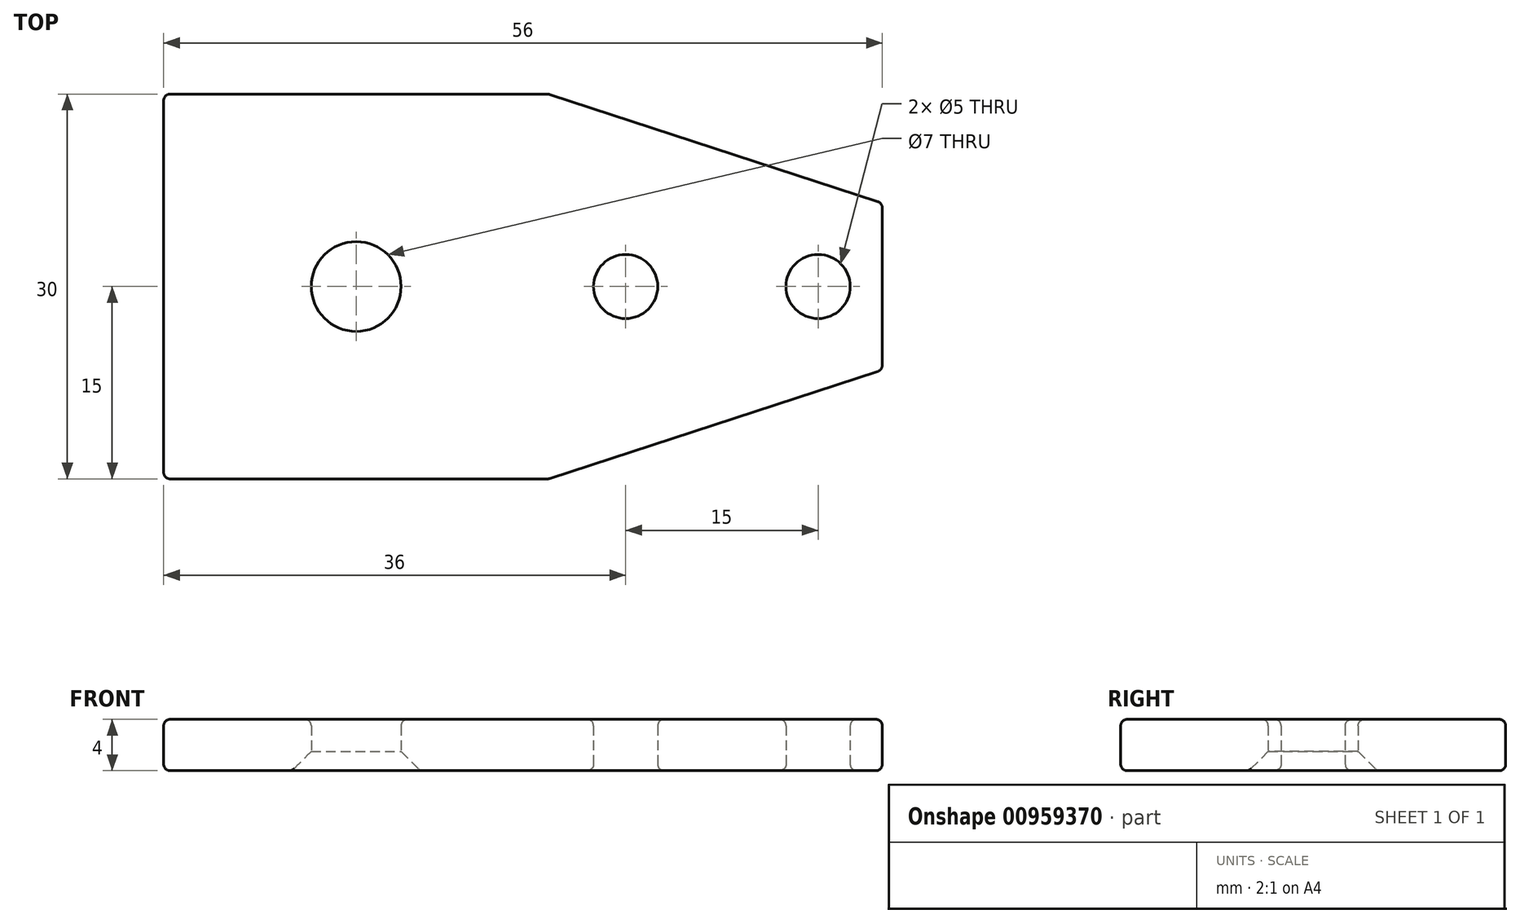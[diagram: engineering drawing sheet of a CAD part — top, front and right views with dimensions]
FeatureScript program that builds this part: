
annotation { "Feature Type Name" : "Feature", "Feature Type Description" : "" }
export const myFeature = defineFeature(function(context is Context, id is Id, definition is map)
    precondition{}
    {
        {
            var Q0;
            Q0=qCreatedBy(makeId("Top.planeOp"),FACE);
            var sketch = newSketch(context, id + "F0", { "sketchPlane" : qUnion([Q0])});
            skLineSegment(sketch, "E0.bottom", {"start": v(15, -15) * mm, "end": v(-15, -15) * mm});
            skLineSegment(sketch, "E0.top", {"start": v(15, 15) * mm, "end": v(-15, 15) * mm});
            skLineSegment(sketch, "E0.left", {"start": v(15, -15) * mm, "end": v(15, 15) * mm});
            skLineSegment(sketch, "E0.right", {"start": v(-15, -15) * mm, "end": v(-15, 15) * mm});
            skPoint(sketch, "E0.middle", {"position": v(0, 0) * mm});
            skLineSegment(sketch, "E1", {"start": v(15, -15) * mm, "end": v(41, -6.5) * mm});
            skLineSegment(sketch, "E2", {"start": v(41, -6.5) * mm, "end": v(41, 6.5) * mm});
            skLineSegment(sketch, "E3", {"start": v(41, 6.5) * mm, "end": v(15, 15) * mm});
            skPoint(sketch, "E4", {"position": v(41, 0) * mm});
            skLineSegment(sketch, "E5", {"start": v(41, 0) * mm, "end": v(0, 0) * mm, "construction": true});
            skPoint(sketch, "E6", {"position": v(36, 0) * mm});
            skPoint(sketch, "E7", {"position": v(21, 0) * mm});
            skSolve(sketch);
        }
        {
            var Q0;
            Q0=makeQuery(id+"F0.imprint","IMPRINT",FACE,{"disambiguationData":[TD([[makeQuery(id+"F0.imprint","IMPRINT",EDGE,{"derivedFrom":sQuery(id+"F0.wireOp",EDGE,"E0.bottom")}),-1.0]])]});
            var Q1;
            Q1=makeQuery(id+"F0.imprint","IMPRINT",FACE,{"disambiguationData":[TD([[makeQuery(id+"F0.imprint","IMPRINT",EDGE,{"derivedFrom":sQuery(id+"F0.wireOp",EDGE,"E0.left")}),-1.0]])]});
            extrude(context, id + "F1", {"entities" : qUnion([Q0, Q1]), "depth" : 4 * mm, "offsetDistance" : 25 * mm});
        }
        {
            var Q0;
            Q0=sQuery(id+"F0.wireOp",VERTEX,"E0.middle");
            var Q1;
            Q1=makeQuery(id+"F1.opExtrude","SWEPT_BODY",BODY,{"disambiguationData":[OSD([sQuery(id+"F0.wireOp",EDGE,"E0.bottom"),sQuery(id+"F0.wireOp",EDGE,"E0.top"),sQuery(id+"F0.wireOp",EDGE,"E0.right"),sQuery(id+"F0.wireOp",EDGE,"E1"),sQuery(id+"F0.wireOp",EDGE,"E2"),sQuery(id+"F0.wireOp",EDGE,"E3")])]});
            hole(context, id + "F2", {"style" : HoleStyle.C_SINK, "endStyle" : HoleEndStyle.THROUGH, "oppositeDirection" : true, "holeDiameter" : 7 * mm, "cSinkDiameter" : 10 * mm, "cSinkAngle" : 90 * degree, "majorDiameter" : 5 * mm, "isTappedThrough" : true, "tappedDepth" : 12 * mm, "tapClearance" : 3, "locations" : qUnion([Q0]), "scope" : qUnion([Q1])});
        }
        {
            var Q0;
            Q0=sQuery(id+"F0.wireOp",VERTEX,"E7");
            var Q1;
            Q1=sQuery(id+"F0.wireOp",VERTEX,"E6");
            var Q2;
            Q2=makeQuery(id+"F1.opExtrude","SWEPT_BODY",BODY,{"disambiguationData":[OSD([sQuery(id+"F0.wireOp",EDGE,"E0.bottom"),sQuery(id+"F0.wireOp",EDGE,"E0.top"),sQuery(id+"F0.wireOp",EDGE,"E0.right"),sQuery(id+"F0.wireOp",EDGE,"E1"),sQuery(id+"F0.wireOp",EDGE,"E2"),sQuery(id+"F0.wireOp",EDGE,"E3")])]});
            hole(context, id + "F3", {"style" : HoleStyle.SIMPLE, "endStyle" : HoleEndStyle.THROUGH, "oppositeDirection" : true, "holeDiameter" : 5 * mm, "majorDiameter" : 5 * mm, "isTappedThrough" : true, "tappedDepth" : 12 * mm, "tapClearance" : 3, "locations" : qUnion([Q0, Q1]), "scope" : qUnion([Q2])});
        }
        {
            var Q0;
            Q0=makeQuery(id+"F1.opExtrude","CAP_FACE",FACE,{"disambiguationData":[OSD([sQuery(id+"F0.wireOp",EDGE,"E0.bottom"),sQuery(id+"F0.wireOp",EDGE,"E0.top"),sQuery(id+"F0.wireOp",EDGE,"E0.right"),sQuery(id+"F0.wireOp",EDGE,"E1"),sQuery(id+"F0.wireOp",EDGE,"E2"),sQuery(id+"F0.wireOp",EDGE,"E3")])],"isStart":true});
            var Q1;
            Q1=makeQuery(id+"F1.opExtrude","CAP_FACE",FACE,{"disambiguationData":[OSD([sQuery(id+"F0.wireOp",EDGE,"E0.bottom"),sQuery(id+"F0.wireOp",EDGE,"E0.top"),sQuery(id+"F0.wireOp",EDGE,"E0.right"),sQuery(id+"F0.wireOp",EDGE,"E1"),sQuery(id+"F0.wireOp",EDGE,"E2"),sQuery(id+"F0.wireOp",EDGE,"E3")])],"isStart":false});
            var Q2;
            Q2=makeQuery(id+"F1.opExtrude","SWEPT_FACE",FACE,{"disambiguationData":[OSD([sQuery(id+"F0.wireOp",EDGE,"E3")])]});
            var Q3;
            Q3=makeQuery(id+"F1.opExtrude","SWEPT_FACE",FACE,{"disambiguationData":[OSD([sQuery(id+"F0.wireOp",EDGE,"E1")])]});
            var Q4;
            Q4=makeQuery(id+"F1.opExtrude","SWEPT_FACE",FACE,{"disambiguationData":[OSD([sQuery(id+"F0.wireOp",EDGE,"E0.bottom")])]});
            var Q5;
            Q5=makeQuery(id+"F1.opExtrude","SWEPT_FACE",FACE,{"disambiguationData":[OSD([sQuery(id+"F0.wireOp",EDGE,"E0.right")])]});
            fillet(context, id + "F4", {"entities" : qUnion([Q0, Q1, Q2, Q3, Q4, Q5]), "tangentPropagation" : true, "radius" : 0.5 * mm, "defaultsChanged" : true, "vertexSettings" : [], "allowEdgeOverflow" : false});
        }
    });
